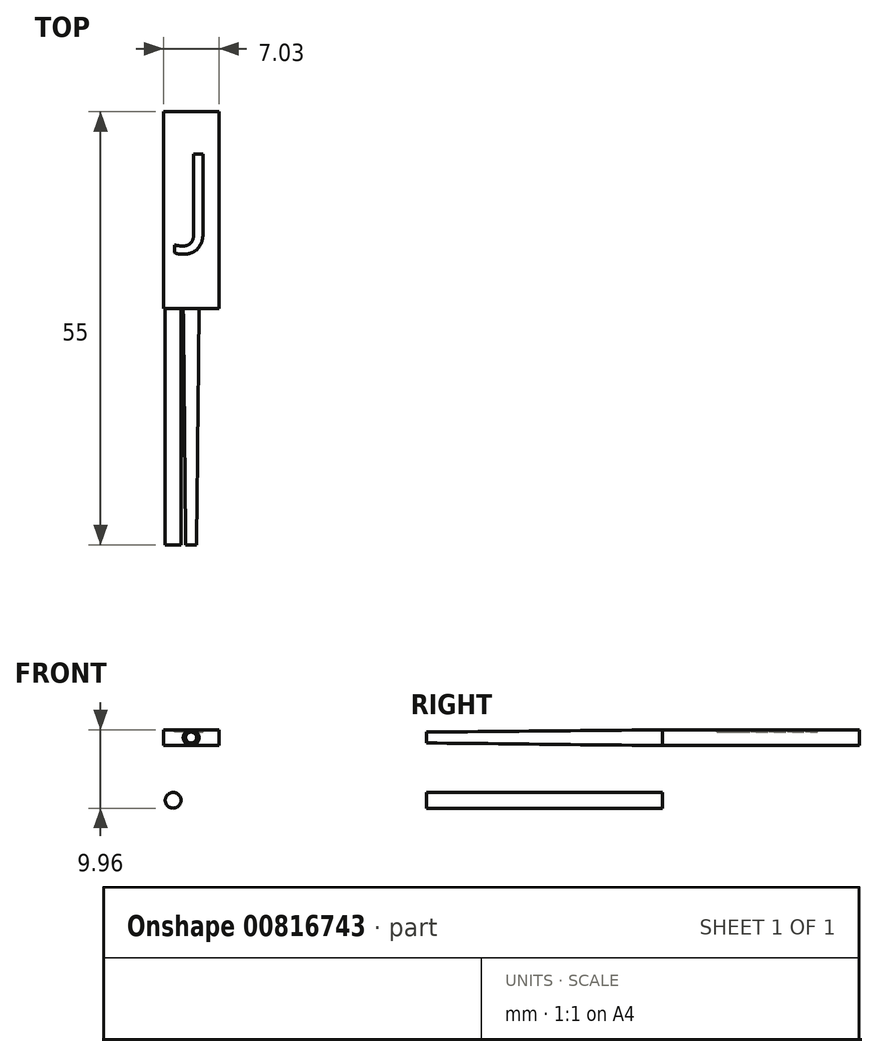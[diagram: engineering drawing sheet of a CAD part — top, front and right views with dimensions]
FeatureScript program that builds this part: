
annotation { "Feature Type Name" : "Feature", "Feature Type Description" : "" }
export const myFeature = defineFeature(function(context is Context, id is Id, definition is map)
    precondition{}
    {
        {
            var Q0;
            Q0=qCreatedBy(makeId("Front.planeOp"),FACE);
            var sketch = newSketch(context, id + "F0", { "sketchPlane" : qUnion([Q0])});
            skCircle(sketch, "E0", {"center": v(-50.6, 19.94) * mm, "radius": 1 * mm});
            skCircle(sketch, "E1", {"center": v(-48.31, 27.9) * mm, "radius": 1 * mm});
            skLineSegment(sketch, "E2.bottom", {"start": v(-51.83, 28.9) * mm, "end": v(-44.8, 28.9) * mm});
            skLineSegment(sketch, "E2.top", {"start": v(-51.83, 26.89) * mm, "end": v(-44.8, 26.89) * mm});
            skLineSegment(sketch, "E2.left", {"start": v(-51.83, 28.9) * mm, "end": v(-51.83, 26.89) * mm});
            skLineSegment(sketch, "E2.right", {"start": v(-44.8, 28.9) * mm, "end": v(-44.8, 26.89) * mm});
            skSolve(sketch);
        }
        {
            var Q0;
            Q0=makeQuery(id+"F0.imprint","IMPRINT",FACE,{"disambiguationData":[TD([[makeQuery(id+"F0.imprint","IMPRINT",EDGE,{"derivedFrom":sQuery(id+"F0.wireOp",EDGE,"E0")}),1.0]])]});
            extrude(context, id + "F1", {"entities" : qUnion([Q0]), "depth" : 30 * mm, "offsetDistance" : 25 * mm});
        }
        {
            var Q0;
            Q0=makeQuery(id+"F1.opExtrude","CAP_FACE",FACE,{"disambiguationData":[OSD([sQuery(id+"F0.wireOp",EDGE,"E0")])],"isStart":false});
            var sketch = newSketch(context, id + "F2", { "sketchPlane" : qUnion([Q0])});
            skCircle(sketch, "E3", {"center": v(-50.6, 19.94) * mm, "radius": 0.7 * mm});
            skCircle(sketch, "E4", {"center": v(-48.32, 27.91) * mm, "radius": 0.7 * mm});
            skSolve(sketch);
        }
        {
            var Q1;
            Q1=makeQuery(id+"F0.imprint","IMPRINT",FACE,{"disambiguationData":[TD([[makeQuery(id+"F0.imprint","IMPRINT",EDGE,{"derivedFrom":sQuery(id+"F0.wireOp",EDGE,"E1")}),1.0]])]});
            var Q2;
            Q2=makeQuery(id+"F2.imprint","IMPRINT",FACE,{"disambiguationData":[TD([[makeQuery(id+"F2.imprint","IMPRINT",EDGE,{"derivedFrom":sQuery(id+"F2.wireOp",EDGE,"E4")}),1.0]])]});
            loft(context, id + "F3", {"sheetProfilesArray" : [{ "sheetProfileEntities" : qUnion([Q1]) }, { "sheetProfileEntities" : qUnion([Q2]) }]});
        }
        {
            var Q0;
            Q0=makeQuery(id+"F0.imprint","IMPRINT",FACE,{"disambiguationData":[TD([[makeQuery(id+"F0.imprint","IMPRINT",EDGE,{"derivedFrom":sQuery(id+"F0.wireOp",EDGE,"E1")}),-1.0]])]});
            var Q1;
            Q1=makeQuery(id+"F0.imprint","IMPRINT",FACE,{"disambiguationData":[TD([[makeQuery(id+"F0.imprint","IMPRINT",EDGE,{"derivedFrom":sQuery(id+"F0.wireOp",EDGE,"E1")}),1.0]])]});
            extrude(context, id + "F4", {"entities" : qUnion([Q0, Q1]), "operationType" : NewBodyOperationType.ADD, "oppositeDirection" : true, "depth" : 25 * mm, "offsetDistance" : 25 * mm});
        }
        {
            var Q0;
            Q0=makeQuery(id+"F4.opExtrude","SWEPT_FACE",FACE,{"disambiguationData":[OSD([sQuery(id+"F0.wireOp",EDGE,"E2.bottom")])]});
            var sketch = newSketch(context, id + "F5", { "sketchPlane" : qUnion([Q0])});
            skPoint(sketch, "E5.firstSnap0", {"position": v(-48.31, 25) * mm});
            skText(sketch, "E6", { "text": "J", "fontName": "OpenSans-Regular.ttf"});
            const initialGuessF5  = {"E6": [-0.04929, 0.00956, 1, 0, 0.01015]};
            skSetInitialGuess(sketch, initialGuessF5);
            skSolve(sketch);
        }
        {
            var Q0;
            Q0=makeQuery(id+"F5.imprint","IMPRINT",FACE,{"disambiguationData":[TD([[makeQuery(id+"F5.imprint","IMPRINT",EDGE,{"derivedFrom":sQuery(id+"F5.wireOp",EDGE,"E6.sketch_text.stroke-0")}),-1.0]])]});
            extrude(context, id + "F6", {"entities" : qUnion([Q0]), "operationType" : NewBodyOperationType.REMOVE, "oppositeDirection" : true, "depth" : 0.3 * mm, "offsetDistance" : 25 * mm});
        }
    });
